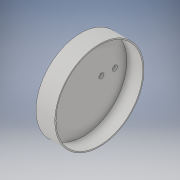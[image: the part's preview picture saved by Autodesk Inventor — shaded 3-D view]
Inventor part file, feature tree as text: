
AUTODESK INVENTOR PART (.ipt)
format: ipt  version: 2019 (Build 230136000, 136)  size: 131,584 bytes
history: native  units: in
note: dims shown in document units (in); Inventor stores cm internally (conversion verified against a paired STEP export)
features: other x3, extrude x2, sketch x1
ambient origin geometry x8: Origin, YZ Plane, XZ Plane, XY Plane, X Axis, Y Axis, Z Axis, Center Point
bodies: Solid1 (feature_tree)
feature tree (6):
  other  "top base"
  extrude  "top outer wall"  Depth=0.7in
  extrude  "Top holes"  Depth=1.95in
  sketch  "Sketch1"  dims[d0=0.122in d1=1.87in d2=1.95in d3=90.0deg d4=3.8in d5=0.7in d6=0.0in d7=3.9in d30=0.37in d31=0.315in d32=0.315in d33=3.1547in d36=1.0in d37=0.0in]
  other  "outer wall"
  other  "top circles"
